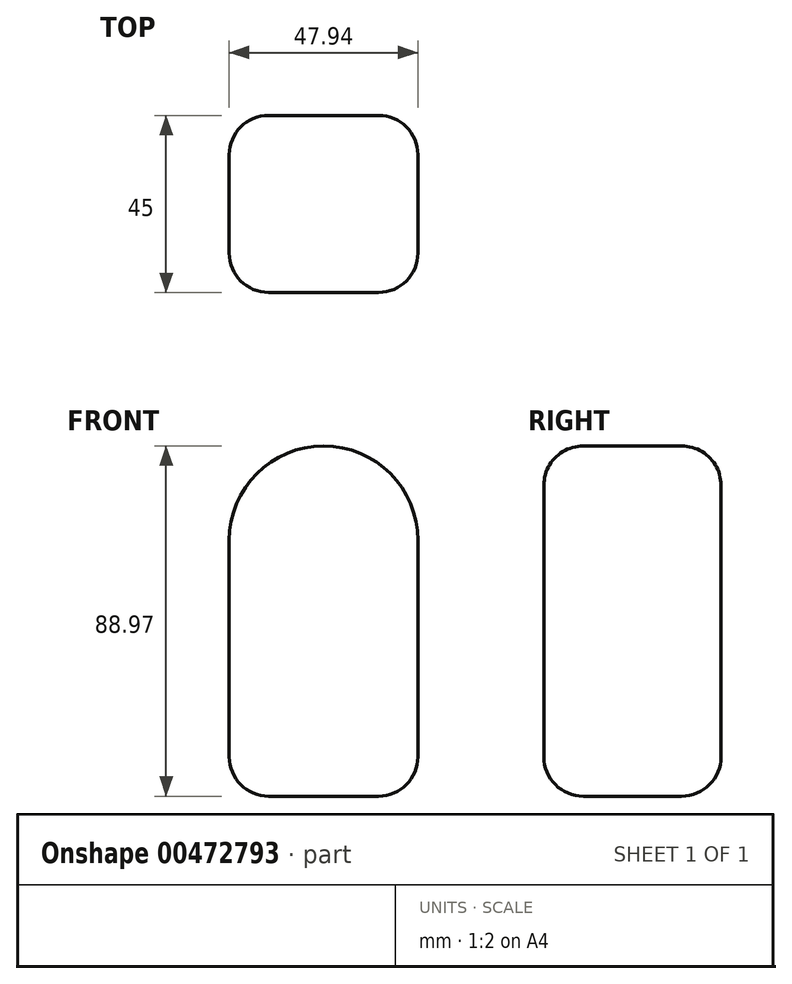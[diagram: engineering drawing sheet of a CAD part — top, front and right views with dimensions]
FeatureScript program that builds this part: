
annotation { "Feature Type Name" : "Feature", "Feature Type Description" : "" }
export const myFeature = defineFeature(function(context is Context, id is Id, definition is map)
    precondition{}
    {
        {
            var Q0;
            Q0=qCreatedBy(makeId("Front.planeOp"),FACE);
            var sketch = newSketch(context, id + "F0", { "sketchPlane" : qUnion([Q0])});
            skLineSegment(sketch, "E0.bottom", {"start": v(23.97, -32.5) * mm, "end": v(-23.97, -32.5) * mm});
            skLineSegment(sketch, "E0.left", {"start": v(23.97, -32.5) * mm, "end": v(23.97, 32.5) * mm});
            skLineSegment(sketch, "E0.right", {"start": v(-23.97, -32.5) * mm, "end": v(-23.97, 32.5) * mm});
            skPoint(sketch, "E0.middle", {"position": v(0, 0) * mm});
            skArc(sketch, "E1", {"start": v(-23.97, 32.5) * mm, "mid": v(0, 56.47) * mm, "end": v(23.97, 32.5) * mm});
            skCircle(sketch, "E2", {"center": v(0, 32.5) * mm, "radius": 19.5 * mm});
            skSolve(sketch);
        }
        {
            var Q0;
            Q0=makeQuery(id+"F0.imprint","IMPRINT",FACE,{"disambiguationData":[TD([[makeQuery(id+"F0.imprint","IMPRINT",EDGE,{"derivedFrom":sQuery(id+"F0.wireOp",EDGE,"E2")}),1.0]])]});
            var Q1;
            Q1=makeQuery(id+"F0.imprint","IMPRINT",FACE,{"disambiguationData":[TD([[makeQuery(id+"F0.imprint","IMPRINT",EDGE,{"derivedFrom":sQuery(id+"F0.wireOp",EDGE,"E0.bottom")}),-1.0]])]});
            extrude(context, id + "F1", {"entities" : qUnion([Q0, Q1]), "endBound" : BoundingType.SYMMETRIC, "depth" : 45 * mm});
        }
        {
            var Q0;
            Q0=makeQuery(id+"F1.opExtrude","CAP_EDGE",EDGE,{"disambiguationData":[OSD([sQuery(id+"F0.wireOp",EDGE,"E0.bottom")])],"isStart":false});
            var Q1;
            Q1=makeQuery(id+"F1.opExtrude","CAP_EDGE",EDGE,{"disambiguationData":[OSD([sQuery(id+"F0.wireOp",EDGE,"E0.right")])],"isStart":false});
            var Q2;
            Q2=makeQuery(id+"F1.opExtrude","SWEPT_EDGE",EDGE,{"disambiguationData":[OSD([sQuery(id+"F0.wireOp",EDGE,"E0.bottom"),sQuery(id+"F0.wireOp",EDGE,"E0.left")])]});
            var Q3;
            Q3=makeQuery(id+"F1.opExtrude","SWEPT_EDGE",EDGE,{"disambiguationData":[OSD([sQuery(id+"F0.wireOp",EDGE,"E0.bottom"),sQuery(id+"F0.wireOp",EDGE,"E0.right")])]});
            var Q4;
            Q4=makeQuery(id+"F1.opExtrude","CAP_EDGE",EDGE,{"disambiguationData":[OSD([sQuery(id+"F0.wireOp",EDGE,"E0.left")])],"isStart":true});
            var Q5;
            Q5=makeQuery(id+"F1.opExtrude","CAP_EDGE",EDGE,{"disambiguationData":[OSD([sQuery(id+"F0.wireOp",EDGE,"E0.bottom")])],"isStart":true});
            fillet(context, id + "F2", {"entities" : qUnion([Q0, Q1, Q2, Q3, Q4, Q5]), "radius" : 10 * mm, "tangentPropagation" : true, "allowEdgeOverflow" : false});
        }
    });
